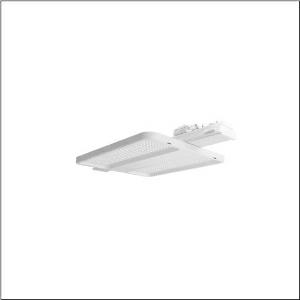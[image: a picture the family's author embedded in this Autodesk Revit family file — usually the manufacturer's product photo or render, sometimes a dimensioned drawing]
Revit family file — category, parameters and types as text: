
# Revit family: highbay_21_fur_licross_r__tragschiene_midi_52hn11da4lla_3016
name_source: partatom
category: Lighting Fixtures
units: mm (PartAtom-declared; Revit-internal decimal feet)

## family parameters
Cut with Voids When Loaded = No
Host = Face
Light Source = No
Part Type = Normal
Room Calculation Point = No
Round Connector Dimension = Use Diameter
Shared = No

## types (1)
- --- (1 x LED, 26500 lm, 142.6 W, 4000K)
    Apparent Load = 143 VA
    CIE Flux Codes = 89 97 99 100 100
    Color Rendering = 80
    Color Temperature = 4000K
    Default Elevation = 1800 mm
    Description = Highbay 21 for Licross® trunking rail midi, high bay luminaire, primary light control with lens, of PMMA, primary optical cover: cover, of PMMA, light emission: direct distribution, primary light characteristic: symmetric, LED, rated luminous flux: 26.500lm, luminous efficacy: 186lm/W, light colour: 840, colour temperature: 4000K, control gear: DALI 2, with plug, 5-pole, with phase selection, mains connection: 230..240V, AC, 50/60Hz, rated input power: 142.6W, housing frame, of high-performance plastic PA6, matt traffic white (RAL 9016), length: 750mm, width: 442mm, height: 71mm, lever catch, fixing on rail side, of steel, galvanised, white, blank cover, of PC/ABS, traffic white (RAL 9016), protection rating (complete): IP64, insulation class (complete): insulation class I (protective earthing), certification: CE, ENEC, VDE, UKCA, protection symbol: D, impact resistance: IK07, permissible operating ambient temperature: -40..+55°C, LABS conformity tested according to VDMA 24364:2018-05, corresponds to IFS (International Featured Standards) requirements for safety and quality in the food industry, packaging unit: 1 piece
    Height = 72 mm  [stored 0.23622 ft]
    Lamp = 1 x LED
    Lamp Light Flux = 26500 lm
    Lamp Power = 142.6 W
    Lamp count = 1
    Length = 474 mm
    Luminous efficacy = 186 lm/W
    Manufacturer = Siteco
    ModVariant = No
    Model = 52HN11DA4LLA
    Mounting Place = Ceiling
    Mounting Type = Pendant
    Number of Poles = 1
    OnlyDefault = Yes
    Power Factor = 1
    Product Name = Highbay 21 für Licross® Tragschiene midi
    Product group = high bay luminaire
    ProductGroupID = 901
    Protection Class = Protection class I
    Protection Degree = IP 64
    RLX_Detail_Level = 1
    RLX_Emergency_Light_Flux = 0 lm
    RLX_Emergency_Type = 0
    RLX_Emergency_Type_DB = No
    RlxData = <blob elided: 17701 chars, md5=97992e5d>
    Socket = socket
    Standby Power = 0 W
    System Light Flux = 26499 lm
    System Power = 143 W
    Type Comments = factory setting: luminous flux: 100 % | dim-lin: 254 | 652 mA
    Type Image = l_1363258.jpg
    URL = http://relux.com
    VarID = @adj_000085
    Voltage = 0 V
    Weight = 0.00 kg
    Width = 442 mm

note: [stored X ft] marks values corroborated as IEEE doubles in the binary element streams (Revit-internal decimal feet)

## geometry (parser evidence)
native form markers: Blend x4, Sweep x10
no freeform markers — native parametric forms only
